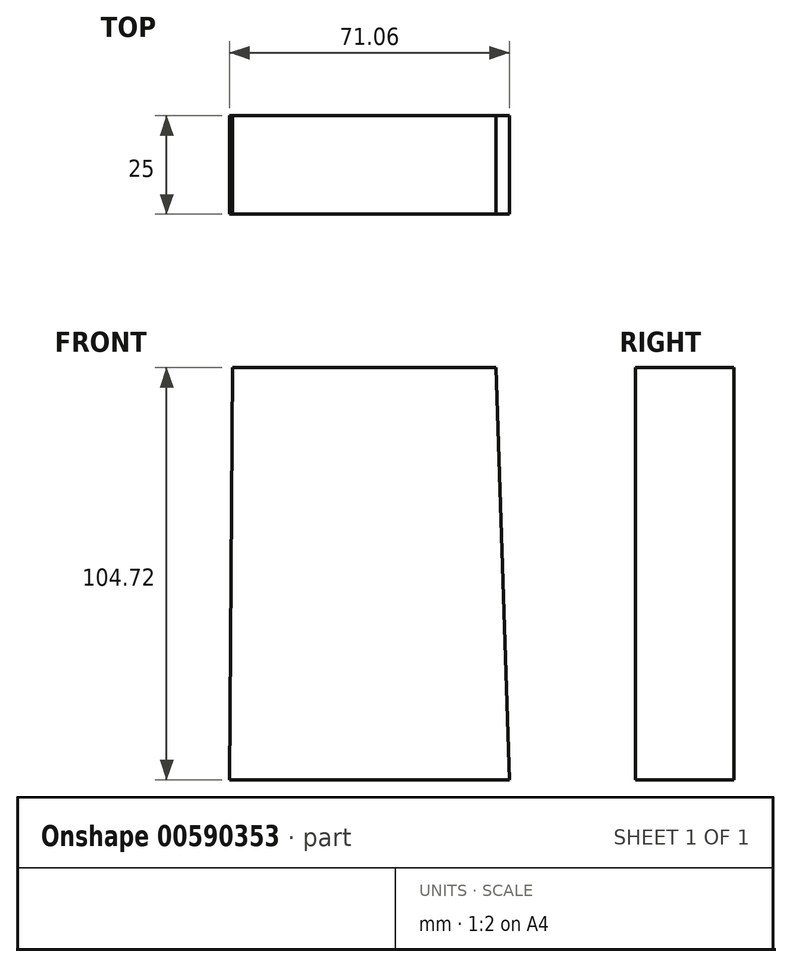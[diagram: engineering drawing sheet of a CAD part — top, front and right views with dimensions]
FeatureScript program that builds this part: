
annotation { "Feature Type Name" : "Feature", "Feature Type Description" : "" }
export const myFeature = defineFeature(function(context is Context, id is Id, definition is map)
    precondition{}
    {
        {
            var Q0;
            Q0=qCreatedBy(makeId("Front.planeOp"),FACE);
            var sketch = newSketch(context, id + "F0", { "sketchPlane" : qUnion([Q0])});
            skLineSegment(sketch, "E0", {"start": v(-32.6, 74.27) * mm, "end": v(34.3, 74.27) * mm});
            skLineSegment(sketch, "E1", {"start": v(34.3, 74.27) * mm, "end": v(37.73, -30.45) * mm});
            skLineSegment(sketch, "E2", {"start": v(37.73, -30.45) * mm, "end": v(-33.33, -30.45) * mm});
            skLineSegment(sketch, "E3", {"start": v(-32.6, 74.27) * mm, "end": v(-33.33, -30.45) * mm});
            skSolve(sketch);
        }
        {
            var Q0;
            Q0=makeQuery(id+"F0.imprint","IMPRINT",FACE,{"disambiguationData":[TD([[makeQuery(id+"F0.imprint","IMPRINT",EDGE,{"derivedFrom":sQuery(id+"F0.wireOp",EDGE,"E0")}),-1.0]])]});
            extrude(context, id + "F1", {"entities" : qUnion([Q0]), "endBound" : BoundingType.SYMMETRIC, "depth" : 25 * mm, "offsetDistance" : 25 * mm});
        }
    });
